# Revit family: EKF_EE_КорпусОднодверныйFORT_IP54_PROxima
name_source: partatom
category: Электрооборудование
units: mm (PartAtom-declared; Revit-internal decimal feet)

## family parameters
Всегда вертикально = Нет
На основе рабочей плоскости = Да
Общий = Да
При загрузке вырезать с полостями = Нет
Размер круглого соединителя = Использовать диаметр
Тип детали = Силовой щит
Точка расчета площади = Нет

## types (25) — shared parameters
ADSK_Единица измерения = шт.
ADSK_Завод-изготовитель = EKF
ADSK_Количество = 1
ADSK_Материал = RAL 7035_Сталь
D = 10 мм
Дверь_t = 21 мм
ЗадняяПанель_t = 24 мм
Изготовитель = EKF
КолОтв = 4
Крышка_t = 14 мм
Отступ = 20 мм
Серия номенклатуры = PROxima
Степень защиты IP = IP54
ТВ = EKF_2
Тип установки = Напольный
zero-valued in all types: ADSK_Масса, Отметка по умолчанию

## per-type parameters (varying)
| type | ADSK_Код изделия | ADSK_Марка | ADSK_Наименование | ADSK_Обозначение | ADSK_Размер_Высота | ADSK_Размер_Глубина | ADSK_Размер_Ширина | Каркас_h | Каркас_Глубина | Тип |
| Корпус FORT IP54 (1800x600x400) EKF PROxima | FK1864G | Корпус FORT | Корпус FORT IP54 (1800x600x400) EKF PROxima | Корпус FORT | 1800 мм | 400 мм | 600 мм | 1786 мм | 350.5 мм | 219 мм |
| Корпус FORT IP54 (1800x600x600) EKF PROxima | FK1866G | Корпус FORT | Корпус FORT IP54 (1800x600x600) EKF PROxima | Корпус FORT | 1800 мм | 600 мм | 600 мм | 1786 мм | 550.5 мм | 220 мм |
| Корпус FORT IP54 (1800x600x800) EKF PROxima | FK1868G | Корпус FORT | Корпус FORT IP54 (1800x600x800) EKF PROxima | Корпус FORT | 1800 мм | 800 мм | 600 мм | 1786 мм | 750.5 мм | 221 мм |
| Корпус FORT IP54 (1800x800x400) EKF PROxima | FK1884G | Корпус FORT | Корпус FORT IP54 (1800x800x400) EKF PROxima | Корпус FORT | 1800 мм | 400 мм | 800 мм | 1786 мм | 350.5 мм | 222 мм |
| Корпус FORT IP54 (1800x800x600) EKF PROxima | FK1886G | Корпус FORT | Корпус FORT IP54 (1800x800x600) EKF PROxima | Корпус FORT | 1800 мм | 600 мм | 800 мм | 1786 мм | 550.5 мм | 223 мм |
| Корпус FORT IP54 (1800x800x800) EKF PROxima | FK1888G | Корпус FORT | Корпус FORT IP54 (1800x800x800) EKF PROxima | Корпус FORT | 1800 мм | 800 мм | 800 мм | 1786 мм | 750.5 мм | 224 мм |
| Корпус FORT IP54 (2000x400x400) EKF PROxima | FK2044G | Корпус FORT | Корпус FORT IP54 (2000x400x400) EKF PROxima | Корпус FORT | 2000 мм | 400 мм | 400 мм | 1986 мм | 350.5 мм | 228 мм |
| Корпус FORT IP54 (2000x400x600) EKF PROxima | FK2046G | Корпус FORT | Корпус FORT IP54 (2000x400x600) EKF PROxima | Корпус FORT | 2000 мм | 600 мм | 400 мм | 1986 мм | 550.5 мм | 229 мм |
| Корпус FORT IP54 (2000x400x800) EKF PROxima | FK2048G | Корпус FORT | Корпус FORT IP54 (2000x400x800) EKF PROxima | Корпус FORT | 2000 мм | 800 мм | 400 мм | 1986 мм | 750.5 мм | 230 мм |
| Корпус FORT IP54 (2000x600x400) EKF PROxima | FK2064G | Корпус FORT | Корпус FORT IP54 (2000x600x400) EKF PROxima | Корпус FORT | 2000 мм | 400 мм | 600 мм | 1986 мм | 350.5 мм | 231 мм |
| Корпус FORT IP54 (2000x600x600) EKF PROxima | FK2066G | Корпус FORT | Корпус FORT IP54 (2000x600x600) EKF PROxima | Корпус FORT | 2000 мм | 600 мм | 600 мм | 1986 мм | 550.5 мм | 232 мм |
| Корпус FORT IP54 (2000x600x800) EKF PROxima | FK2068G | Корпус FORT | Корпус FORT IP54 (2000x600x800) EKF PROxima | Корпус FORT | 2000 мм | 800 мм | 600 мм | 1986 мм | 750.5 мм | 233 мм |
| Корпус FORT IP54 (2000x800x400) EKF PROxima | FK2084G | Корпус FORT | Корпус FORT IP54 (2000x800x400) EKF PROxima | Корпус FORT | 2000 мм | 400 мм | 800 мм | 1986 мм | 350.5 мм | 234 мм |
| Корпус FORT IP54 (2000x800x600) EKF PROxima | FK2086G | Корпус FORT | Корпус FORT IP54 (2000x800x600) EKF PROxima | Корпус FORT | 2000 мм | 600 мм | 800 мм | 1986 мм | 550.5 мм | 235 мм |
| Корпус FORT IP54 (2000x800x800) EKF PROxima | FK2088G | Корпус FORT | Корпус FORT IP54 (2000x800x800) EKF PROxima | Корпус FORT | 2000 мм | 800 мм | 800 мм | 1986 мм | 750.5 мм | 236 мм |
| Корпус FORT IP54 (2200x400x400) EKF PROxima | FK2244G | Корпус FORT | Корпус FORT IP54 (2200x400x400) EKF PROxima | Корпус FORT | 2200 мм | 400 мм | 400 мм | 2186 мм | 350.5 мм | 240 мм |
| Корпус FORT IP54 (2200x400x600) EKF PROxima | FK2246G | Корпус FORT | Корпус FORT IP54 (2200x400x600) EKF PROxima | Корпус FORT | 2200 мм | 600 мм | 400 мм | 2186 мм | 550.5 мм | 241 мм |
| Корпус FORT IP54 (2200x400x800) EKF PROxima | FK2248G | Корпус FORT | Корпус FORT IP54 (2200x400x800) EKF PROxima | Корпус FORT | 2200 мм | 800 мм | 400 мм | 2186 мм | 750.5 мм | 242 мм |
| Корпус FORT IP54 (2200x600x400) EKF PROxima | FK2264G | Корпус FORT | Корпус FORT IP54 (2200x600x400) EKF PROxima | Корпус FORT | 2200 мм | 400 мм | 600 мм | 2186 мм | 350.5 мм | 243 мм |
| Корпус FORT IP54 (2200x600x600) EKF PROxima | FK2266G | Корпус FORT | Корпус FORT IP54 (2200x600x600) EKF PROxima | Корпус FORT | 2200 мм | 600 мм | 600 мм | 2186 мм | 550.5 мм | 244 мм |
| Корпус FORT IP54 (2200x600x800) EKF PROxima | FK2268G | Корпус FORT | Корпус FORT IP54 (2200x600x800) EKF PROxima | Корпус FORT | 2200 мм | 800 мм | 600 мм | 2186 мм | 750.5 мм | 245 мм |
| Корпус FORT IP54 (2200x800x400) EKF PROxima | FK2284G | Корпус FORT | Корпус FORT IP54 (2200x800x400) EKF PROxima | Корпус FORT | 2200 мм | 400 мм | 800 мм | 2186 мм | 350.5 мм | 246 мм |
| Корпус FORT IP54 (2200x800x600) EKF PROxima | FK2286G | Корпус FORT | Корпус FORT IP54 (2200x800x600) EKF PROxima | Корпус FORT | 2200 мм | 600 мм | 800 мм | 2186 мм | 550.5 мм | 247 мм |
| Корпус FORT IP54 (2200x800x800) EKF PROxima | FK2288G | Корпус FORT | Корпус FORT IP54 (2200x800x800) EKF PROxima | Корпус FORT | 2200 мм | 800 мм | 800 мм | 2186 мм | 750.5 мм | 248 мм |
| Корпус FORT IP54 с окном под вент. (1800x800x600) EKF PROxima | FK1886GAZ | Корпус FORT с окном под вент. | Корпус FORT IP54 с окном под вент.  (1800x800x600) EKF PROxima | Корпус FORT с окном под вент. | 2200 мм | 800 мм | 800 мм | 2186 мм | 750.5 мм | 249 мм |
